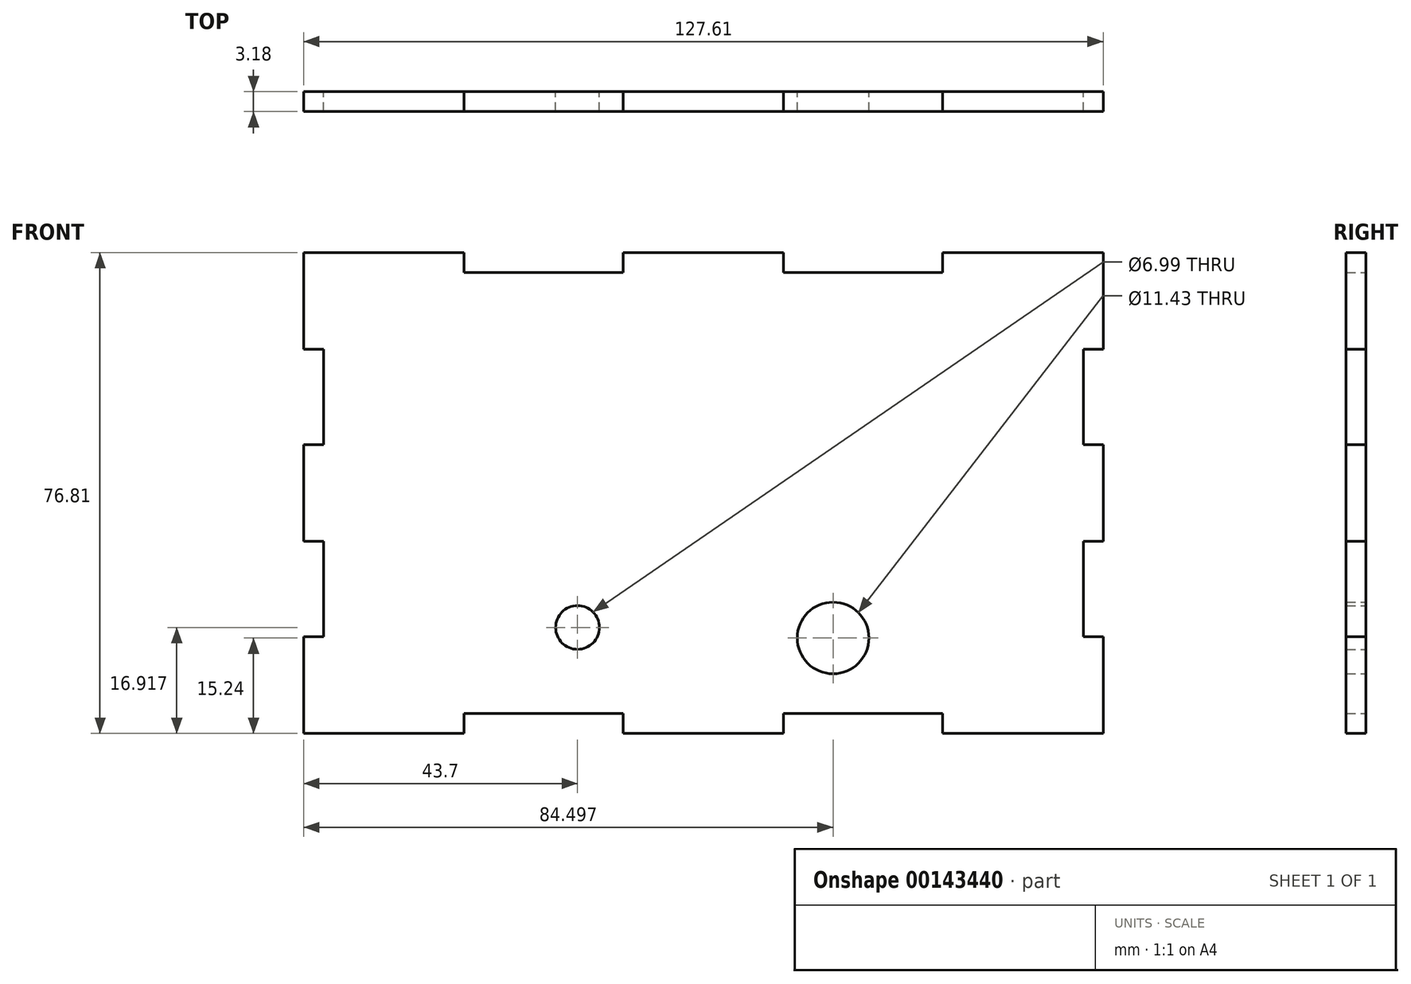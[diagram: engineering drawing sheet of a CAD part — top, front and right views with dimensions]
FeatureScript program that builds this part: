
annotation { "Feature Type Name" : "Feature", "Feature Type Description" : "" }
export const myFeature = defineFeature(function(context is Context, id is Id, definition is map)
    precondition{}
    {
        {
            var Q0;
            Q0=qCreatedBy(makeId("Front.planeOp"),FACE);
            var sketch = newSketch(context, id + "F0", { "sketchPlane" : qUnion([Q0])});
            skLineSegment(sketch, "E0.bottom", {"start": v(-45.76, 37.37) * mm, "end": v(-20.16, 37.37) * mm});
            skLineSegment(sketch, "E0.top", {"start": v(-45.76, -39.44) * mm, "end": v(-20.16, -39.44) * mm});
            skLineSegment(sketch, "E0.left", {"start": v(-45.76, 37.37) * mm, "end": v(-45.76, 21.93) * mm});
            skLineSegment(sketch, "E0.right", {"start": v(81.85, 37.37) * mm, "end": v(81.85, 21.93) * mm});
            skLineSegment(sketch, "E1.0", {"start": v(78.67, 21.93) * mm, "end": v(78.67, 6.69) * mm});
            skLineSegment(sketch, "E1.2", {"start": v(-42.59, 21.93) * mm, "end": v(-42.59, 6.69) * mm});
            skLineSegment(sketch, "E2.0", {"start": v(-45.76, 21.93) * mm, "end": v(-42.59, 21.93) * mm});
            skLineSegment(sketch, "E3.0", {"start": v(-45.76, 6.69) * mm, "end": v(-42.59, 6.69) * mm});
            skLineSegment(sketch, "E4.0", {"start": v(-45.76, -8.76) * mm, "end": v(-42.59, -8.76) * mm});
            skLineSegment(sketch, "E5.0", {"start": v(-45.76, -24) * mm, "end": v(-42.59, -24) * mm});
            skLineSegment(sketch, "E6.trimOffspring", {"start": v(78.67, 6.69) * mm, "end": v(81.85, 6.69) * mm});
            skLineSegment(sketch, "E7.trimOffspring", {"start": v(78.67, 21.93) * mm, "end": v(81.85, 21.93) * mm});
            skLineSegment(sketch, "E8.trimOffspring", {"start": v(78.67, -8.76) * mm, "end": v(81.85, -8.76) * mm});
            skLineSegment(sketch, "E9.trimOffspring", {"start": v(78.67, -24) * mm, "end": v(81.85, -24) * mm});
            skLineSegment(sketch, "E10.trimOffspring", {"start": v(-45.76, -24) * mm, "end": v(-45.76, -39.44) * mm});
            skLineSegment(sketch, "E11.trimOffspring", {"start": v(-45.76, 6.69) * mm, "end": v(-45.76, -8.76) * mm});
            skLineSegment(sketch, "E12.trimOffspring", {"start": v(81.85, 6.69) * mm, "end": v(81.85, -8.76) * mm});
            skLineSegment(sketch, "E13.trimOffspring", {"start": v(81.85, -24) * mm, "end": v(81.85, -39.44) * mm});
            skLineSegment(sketch, "E14.trimOffspring", {"start": v(78.67, -8.76) * mm, "end": v(78.67, -24) * mm});
            skLineSegment(sketch, "E15.trimOffspring", {"start": v(-42.59, -8.76) * mm, "end": v(-42.59, -24) * mm});
            skLineSegment(sketch, "E16.0", {"start": v(-20.16, 37.37) * mm, "end": v(-20.16, 34.2) * mm});
            skLineSegment(sketch, "E17.0", {"start": v(5.24, 37.37) * mm, "end": v(5.24, 34.2) * mm});
            skLineSegment(sketch, "E18.0", {"start": v(30.84, 37.37) * mm, "end": v(30.84, 34.2) * mm});
            skLineSegment(sketch, "E19.0", {"start": v(56.24, 37.37) * mm, "end": v(56.24, 34.2) * mm});
            skLineSegment(sketch, "E20.0", {"start": v(-20.16, 34.2) * mm, "end": v(5.24, 34.2) * mm});
            skLineSegment(sketch, "E21", {"start": v(-20.16, -36.26) * mm, "end": v(-20.16, -39.44) * mm});
            skLineSegment(sketch, "E22", {"start": v(5.24, -36.26) * mm, "end": v(5.24, -39.44) * mm});
            skLineSegment(sketch, "E23", {"start": v(56.24, -36.26) * mm, "end": v(56.24, -39.44) * mm});
            skLineSegment(sketch, "E24", {"start": v(30.84, -36.26) * mm, "end": v(30.84, -39.44) * mm});
            skLineSegment(sketch, "E25.trimOffspring", {"start": v(5.24, 37.37) * mm, "end": v(30.84, 37.37) * mm});
            skLineSegment(sketch, "E26.trimOffspring", {"start": v(56.24, 37.37) * mm, "end": v(81.85, 37.37) * mm});
            skLineSegment(sketch, "E27.trimOffspring", {"start": v(5.24, -39.44) * mm, "end": v(30.84, -39.44) * mm});
            skLineSegment(sketch, "E28.trimOffspring", {"start": v(56.24, -39.44) * mm, "end": v(81.85, -39.44) * mm});
            skLineSegment(sketch, "E29.trimOffspring", {"start": v(30.84, -36.26) * mm, "end": v(56.24, -36.26) * mm});
            skLineSegment(sketch, "E30.trimOffspring", {"start": v(30.84, 34.2) * mm, "end": v(56.24, 34.2) * mm});
            skLineSegment(sketch, "E31", {"start": v(-20.16, -36.26) * mm, "end": v(5.24, -36.26) * mm});
            skCircle(sketch, "E32", {"center": v(-2.06, -22.52) * mm, "radius": 3.5 * mm});
            skCircle(sketch, "E33", {"center": v(38.74, -24.2) * mm, "radius": 5.72 * mm});
            skSolve(sketch);
        }
        {
            var Q0;
            Q0=makeQuery(id+"F0.imprint","IMPRINT",FACE,{"disambiguationData":[TD([[makeQuery(id+"F0.imprint","IMPRINT",EDGE,{"derivedFrom":sQuery(id+"F0.wireOp",EDGE,"E0.bottom")}),-1.0]])]});
            extrude(context, id + "F1", {"entities" : qUnion([Q0]), "depth" : 3.17 * mm});
        }
    });
